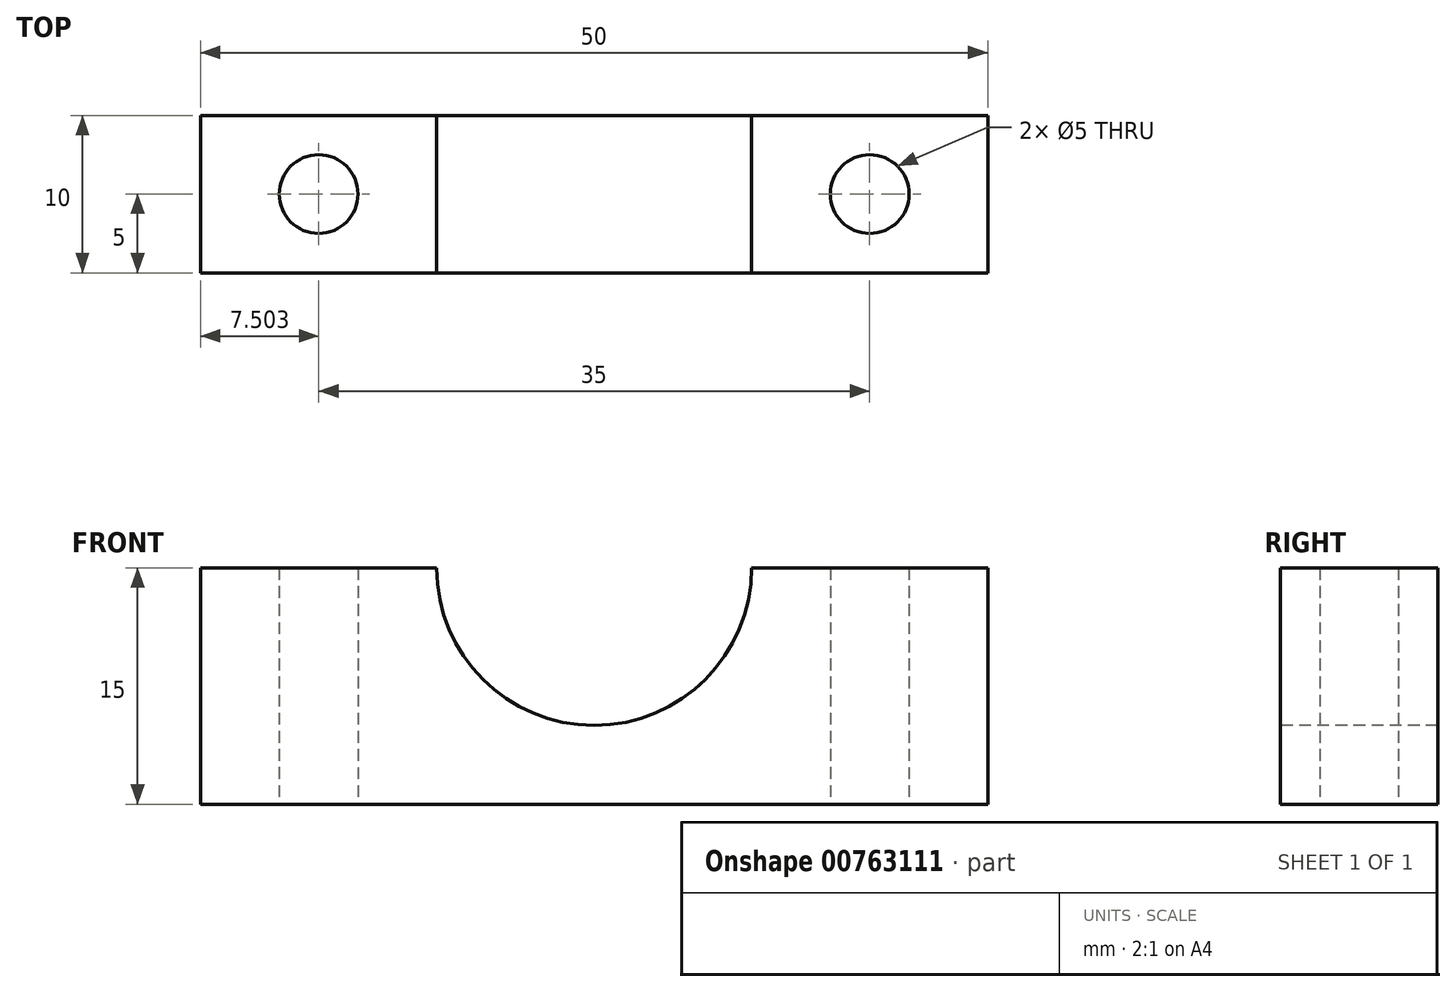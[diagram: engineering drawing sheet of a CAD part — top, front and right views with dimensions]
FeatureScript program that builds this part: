
annotation { "Feature Type Name" : "Feature", "Feature Type Description" : "" }
export const myFeature = defineFeature(function(context is Context, id is Id, definition is map)
    precondition{}
    {
        {
            var Q0;
            Q0=qCreatedBy(makeId("Top.planeOp"),FACE);
            var sketch = newSketch(context, id + "F0", { "sketchPlane" : qUnion([Q0])});
            skLineSegment(sketch, "E0.bottom", {"start": v(-27.9, 10) * mm, "end": v(22.1, 10) * mm});
            skLineSegment(sketch, "E0.top", {"start": v(-27.9, 0) * mm, "end": v(22.1, 0) * mm});
            skLineSegment(sketch, "E0.left", {"start": v(-27.9, 10) * mm, "end": v(-27.9, 0) * mm});
            skLineSegment(sketch, "E0.right", {"start": v(22.1, 10) * mm, "end": v(22.1, 0) * mm});
            skCircle(sketch, "E1", {"center": v(-20.4, 5) * mm, "radius": 2.5 * mm});
            skLineSegment(sketch, "E2", {"start": v(-20.4, 5) * mm, "end": v(-27.9, 5) * mm});
            skCircle(sketch, "E3", {"center": v(14.6, 5) * mm, "radius": 2.5 * mm});
            skLineSegment(sketch, "E4", {"start": v(14.6, 5) * mm, "end": v(22.1, 5) * mm});
            skSolve(sketch);
        }
        {
            var Q0;
            Q0 = qSketchRegion(id + "F0", true);
            extrude(context, id + "F1", {"entities" : qUnion([Q0]), "depth" : 15 * mm, "offsetDistance" : 25 * mm});
        }
        {
            var Q0;
            Q0=qCreatedBy(makeId("Front.planeOp"),FACE);
            var sketch = newSketch(context, id + "F2", { "sketchPlane" : qUnion([Q0])});
            skArc(sketch, "E5", {"start": v(-12.9, 15) * mm, "mid": v(-2.9, 5) * mm, "end": v(7.1, 15) * mm});
            skLineSegment(sketch, "E6", {"start": v(-12.9, 15) * mm, "end": v(7.1, 15) * mm});
            skSolve(sketch);
        }
        {
            var Q0;
            Q0 = qSketchRegion(id + "F2", true);
            extrude(context, id + "F3", {"entities" : qUnion([Q0]), "operationType" : NewBodyOperationType.REMOVE, "oppositeDirection" : true, "depth" : 10 * mm, "offsetDistance" : 25 * mm});
        }
    });
